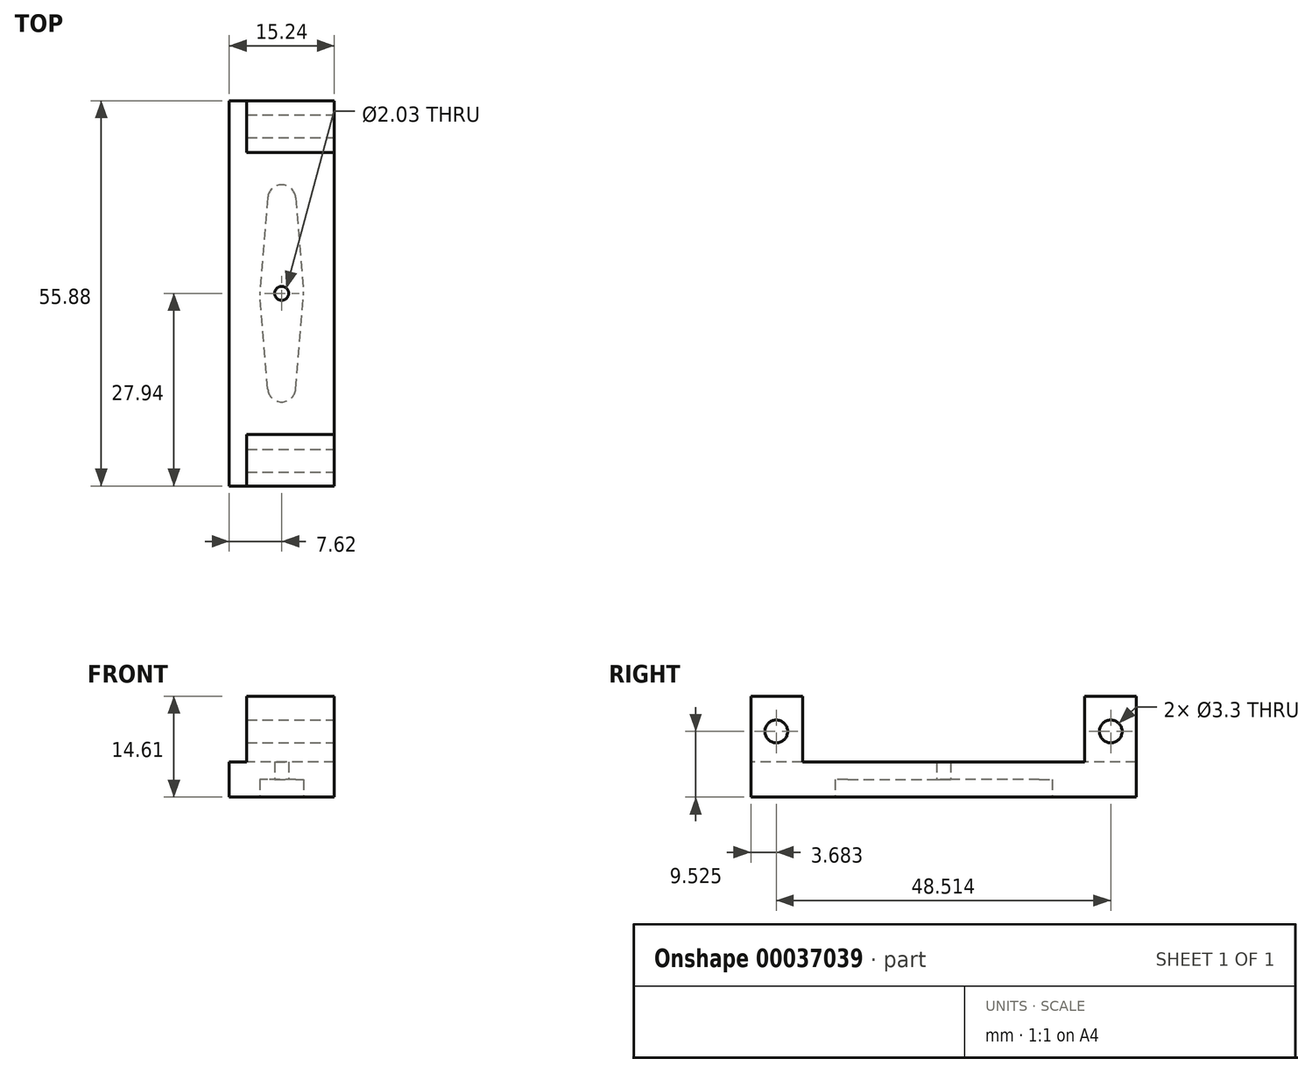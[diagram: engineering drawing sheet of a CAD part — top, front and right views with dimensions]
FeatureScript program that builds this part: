
annotation { "Feature Type Name" : "Feature", "Feature Type Description" : "" }
export const myFeature = defineFeature(function(context is Context, id is Id, definition is map)
    precondition{}
    {
        {
            var Q0;
            Q0=qCreatedBy(makeId("Right.planeOp"),FACE);
            var sketch = newSketch(context, id + "F0", { "sketchPlane" : qUnion([Q0])});
            skLineSegment(sketch, "E0", {"start": v(0, -5.08) * mm, "end": v(27.94, -5.08) * mm});
            skLineSegment(sketch, "E1", {"start": v(27.94, -5.08) * mm, "end": v(27.94, 9.53) * mm});
            skLineSegment(sketch, "E2", {"start": v(27.94, 9.53) * mm, "end": v(20.45, 9.53) * mm});
            skLineSegment(sketch, "E3", {"start": v(20.45, 9.53) * mm, "end": v(20.45, 0) * mm});
            skLineSegment(sketch, "E4", {"start": v(20.45, 0) * mm, "end": v(0, 0) * mm});
            skLineSegment(sketch, "E5", {"start": v(0, 0) * mm, "end": v(0, -5.08) * mm});
            skSolve(sketch);
        }
        {
            var Q0;
            Q0 = qSketchRegion(id + "F0", true);
            extrude(context, id + "F1", {"entities" : qUnion([Q0]), "endBound" : BoundingType.SYMMETRIC, "depth" : 15.24 * mm});
        }
        {
            var Q0;
            Q0=makeQuery(id+"F1.opExtrude","SWEPT_BODY",BODY,{"disambiguationData":[OSD([sQuery(id+"F0.wireOp",EDGE,"E0"),sQuery(id+"F0.wireOp",EDGE,"E1"),sQuery(id+"F0.wireOp",EDGE,"E2"),sQuery(id+"F0.wireOp",EDGE,"E3"),sQuery(id+"F0.wireOp",EDGE,"E4"),sQuery(id+"F0.wireOp",EDGE,"E5")])]});
            var Q1;
            Q1=qCreatedBy(makeId("Front.planeOp"),FACE);
            mirror(context, id + "F2", {"operationType" : NewBodyOperationType.ADD, "entities" : qUnion([Q0]), "mirrorPlane" : qUnion([Q1])});
        }
        {
            var Q0;
            {var subQ0=makeQuery(id+"F1.opExtrude","CAP_FACE",FACE,{"disambiguationData":[OSD([sQuery(id+"F0.wireOp",EDGE,"E0"),sQuery(id+"F0.wireOp",EDGE,"E1"),sQuery(id+"F0.wireOp",EDGE,"E2"),sQuery(id+"F0.wireOp",EDGE,"E3"),sQuery(id+"F0.wireOp",EDGE,"E4"),sQuery(id+"F0.wireOp",EDGE,"E5")])],"isStart":false});Q0=makeQuery(id+"F2.boolean.opBoolean","MERGE",FACE,{"derivedFrom":[subQ0,makeQuery(id+"F2.opPattern","COPY",FACE,{"derivedFrom":subQ0,"instanceName":"1"})]});}
            var sketch = newSketch(context, id + "F3", { "sketchPlane" : qUnion([Q0])});
            skCircle(sketch, "E6", {"center": v(-24.26, 4.44) * mm, "radius": 1.65 * mm});
            skCircle(sketch, "E7", {"center": v(24.26, 4.45) * mm, "radius": 1.65 * mm});
            skLineSegment(sketch, "E8", {"start": v(24.26, 4.45) * mm, "end": v(-24.26, 4.44) * mm, "construction": true});
            skSolve(sketch);
        }
        {
            var Q0;
            Q0 = qSketchRegion(id + "F3", true);
            extrude(context, id + "F4", {"entities" : qUnion([Q0]), "operationType" : NewBodyOperationType.REMOVE, "oppositeDirection" : true, "depth" : 25.4 * mm});
        }
        {
            var Q0;
            {var subQ0=makeQuery(id+"F1.opExtrude","SWEPT_FACE",FACE,{"disambiguationData":[OSD([sQuery(id+"F0.wireOp",EDGE,"E0")])]});Q0=makeQuery(id+"F2.boolean.opBoolean","MERGE",FACE,{"derivedFrom":[subQ0,makeQuery(id+"F2.opPattern","COPY",FACE,{"derivedFrom":subQ0,"instanceName":"1"})]});}
            var sketch = newSketch(context, id + "F5", { "sketchPlane" : qUnion([Q0])});
            skCircle(sketch, "E9", {"center": v(0, 0) * mm, "radius": 3.18 * mm, "construction": true});
            skArc(sketch, "E10", {"start": v(-2.03, -13.88) * mm, "mid": v(0, -15.75) * mm, "end": v(2.03, -13.88) * mm});
            skLineSegment(sketch, "E11", {"start": v(2.03, -13.88) * mm, "end": v(3.16, -0.26) * mm});
            skLineSegment(sketch, "E12", {"start": v(-2.03, -13.88) * mm, "end": v(-3.16, -0.26) * mm});
            skLineSegment(sketch, "E13", {"start": v(0, 0) * mm, "end": v(0, -13.7) * mm, "construction": true});
            skLineSegment(sketch, "E14", {"start": v(3.16, -0.26) * mm, "end": v(-3.16, -0.26) * mm, "construction": true});
            skLineSegment(sketch, "E15.MirrorCS", {"start": v(-2.03, 13.88) * mm, "end": v(-3.16, 0.26) * mm});
            skArc(sketch, "E16.MirrorCS", {"start": v(-2.03, 13.88) * mm, "mid": v(0, 15.75) * mm, "end": v(2.03, 13.88) * mm});
            skLineSegment(sketch, "E17.MirrorCS", {"start": v(2.03, 13.88) * mm, "end": v(3.16, 0.26) * mm});
            skArc(sketch, "E18", {"start": v(3.16, -0.26) * mm, "mid": v(3.18, 0) * mm, "end": v(3.16, 0.26) * mm});
            skArc(sketch, "E19", {"start": v(-3.16, 0.26) * mm, "mid": v(-3.18, 0) * mm, "end": v(-3.16, -0.26) * mm});
            skSolve(sketch);
        }
        {
            var Q0;
            Q0 = qSketchRegion(id + "F5", true);
            extrude(context, id + "F6", {"entities" : qUnion([Q0]), "operationType" : NewBodyOperationType.REMOVE, "oppositeDirection" : true, "depth" : 2.54 * mm});
        }
        {
            var Q0;
            Q0=makeQuery(id+"F6.boolean.opBoolean","COPY",FACE,{"derivedFrom":makeQuery(id+"F6.opExtrude","CAP_FACE",FACE,{"disambiguationData":[OSD([sQuery(id+"F5.wireOp",EDGE,"E10"),sQuery(id+"F5.wireOp",EDGE,"E11"),sQuery(id+"F5.wireOp",EDGE,"E12"),sQuery(id+"F5.wireOp",EDGE,"E15.MirrorCS"),sQuery(id+"F5.wireOp",EDGE,"E16.MirrorCS"),sQuery(id+"F5.wireOp",EDGE,"E17.MirrorCS"),sQuery(id+"F5.wireOp",EDGE,"E18"),sQuery(id+"F5.wireOp",EDGE,"E19")])],"isStart":false})});
            var sketch = newSketch(context, id + "F7", { "sketchPlane" : qUnion([Q0])});
            skPoint(sketch, "E20", {"position": v(0, 0) * mm});
            skSolve(sketch);
        }
        {
            var Q0;
            Q0=sQuery(id+"F7.wireOp",VERTEX,"E20");
            var Q1;
            Q1=makeQuery(id+"F1.opExtrude","SWEPT_BODY",BODY,{"disambiguationData":[OSD([sQuery(id+"F0.wireOp",EDGE,"E0"),sQuery(id+"F0.wireOp",EDGE,"E1"),sQuery(id+"F0.wireOp",EDGE,"E2"),sQuery(id+"F0.wireOp",EDGE,"E3"),sQuery(id+"F0.wireOp",EDGE,"E4"),sQuery(id+"F0.wireOp",EDGE,"E5")])]});
            hole(context, id + "F8", {"style" : HoleStyle.SIMPLE, "holeDiameter" : 2.03 * mm, "endStyle" : HoleEndStyle.THROUGH, "locations" : qUnion([Q0]), "scope" : qUnion([Q1])});
        }
        {
            var Q0;
            {var subQ0=makeQuery(id+"F1.opExtrude","CAP_FACE",FACE,{"disambiguationData":[OSD([sQuery(id+"F0.wireOp",EDGE,"E0"),sQuery(id+"F0.wireOp",EDGE,"E1"),sQuery(id+"F0.wireOp",EDGE,"E2"),sQuery(id+"F0.wireOp",EDGE,"E3"),sQuery(id+"F0.wireOp",EDGE,"E4"),sQuery(id+"F0.wireOp",EDGE,"E5")])],"isStart":true});Q0=makeQuery(id+"F2.boolean.opBoolean","MERGE",FACE,{"derivedFrom":[subQ0,makeQuery(id+"F2.opPattern","COPY",FACE,{"derivedFrom":subQ0,"instanceName":"1"})]});}
            var sketch = newSketch(context, id + "F9", { "sketchPlane" : qUnion([Q0])});
            skLineSegment(sketch, "E21.bottom", {"start": v(-27.94, 9.53) * mm, "end": v(27.94, 9.53) * mm});
            skLineSegment(sketch, "E21.top", {"start": v(-27.94, 0) * mm, "end": v(27.94, 0) * mm});
            skLineSegment(sketch, "E21.left", {"start": v(-27.94, 9.53) * mm, "end": v(-27.94, 0) * mm});
            skLineSegment(sketch, "E21.right", {"start": v(27.94, 9.53) * mm, "end": v(27.94, 0) * mm});
            skSolve(sketch);
        }
        {
            var Q0;
            {var subQ0=makeQuery(id+"F1.opExtrude","CAP_EDGE",EDGE,{"disambiguationData":[OSD([sQuery(id+"F0.wireOp",EDGE,"E3")])],"isStart":true});Q0=makeQuery(id+"F9.imprint","IMPRINT",FACE,{"disambiguationData":[TD([[makeQuery(id+"F9.imprint","IMPRINT",EDGE,{"derivedFrom":subQ0}),1.0]])]});}
            var Q1;
            {var subQ5=sQuery(id+"F9.wireOp",EDGE,"E21.left");Q1=makeQuery(id+"F9.imprint","IMPRINT",FACE,{"disambiguationData":[TD([[makeQuery(id+"F9.imprint","IMPRINT",EDGE,{"derivedFrom":subQ5}),-1.0]])]});}
            var Q2;
            {var subQ5=sQuery(id+"F9.wireOp",EDGE,"E21.right");Q2=makeQuery(id+"F9.imprint","IMPRINT",FACE,{"disambiguationData":[TD([[makeQuery(id+"F9.imprint","IMPRINT",EDGE,{"derivedFrom":subQ5}),1.0]])]});}
            extrude(context, id + "F10", {"entities" : qUnion([Q0, Q1, Q2]), "operationType" : NewBodyOperationType.REMOVE, "oppositeDirection" : true, "depth" : 2.54 * mm});
        }
    });
